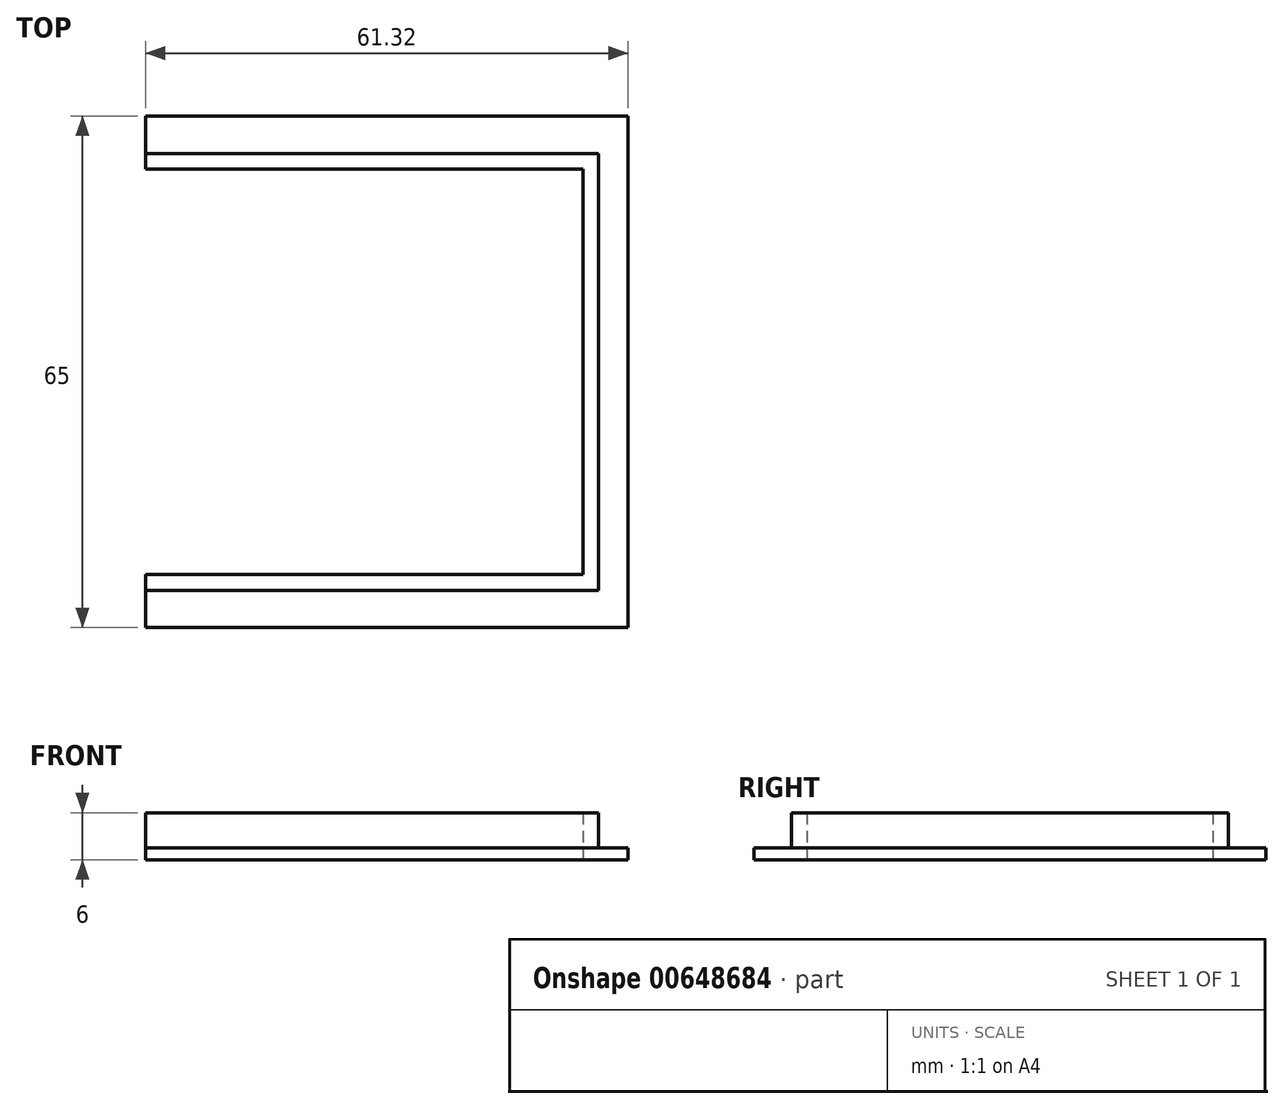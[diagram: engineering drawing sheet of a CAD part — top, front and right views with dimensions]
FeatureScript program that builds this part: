
annotation { "Feature Type Name" : "Feature", "Feature Type Description" : "" }
export const myFeature = defineFeature(function(context is Context, id is Id, definition is map)
    precondition{}
    {
        {
            var Q0;
            Q0=qCreatedBy(makeId("Top.planeOp"),FACE);
            var sketch = newSketch(context, id + "F0", { "sketchPlane" : qUnion([Q0])});
            skLineSegment(sketch, "E0.bottom", {"start": v(29.25, -25.75) * mm, "end": v(-29.25, -25.75) * mm});
            skLineSegment(sketch, "E0.top", {"start": v(29.25, 25.75) * mm, "end": v(-26.32, 25.75) * mm});
            skLineSegment(sketch, "E0.left", {"start": v(29.25, -25.75) * mm, "end": v(29.25, 25.75) * mm});
            skLineSegment(sketch, "E0.right", {"start": v(-29.25, -25.75) * mm, "end": v(-29.25, 25.75) * mm});
            skPoint(sketch, "E0.middle", {"position": v(0, 0) * mm});
            skLineSegment(sketch, "E1.bottom", {"start": v(35, -32.5) * mm, "end": v(-35, -32.5) * mm});
            skLineSegment(sketch, "E1.top", {"start": v(35, 32.5) * mm, "end": v(-26.32, 32.5) * mm});
            skLineSegment(sketch, "E1.left", {"start": v(35, -32.5) * mm, "end": v(35, 32.5) * mm});
            skLineSegment(sketch, "E1.right", {"start": v(-35, -32.5) * mm, "end": v(-35, 32.5) * mm});
            skLineSegment(sketch, "E2.0", {"start": v(-31.25, -27.75) * mm, "end": v(-31.25, 27.75) * mm});
            skLineSegment(sketch, "E2.1", {"start": v(31.25, -27.75) * mm, "end": v(-31.25, -27.75) * mm});
            skLineSegment(sketch, "E2.2", {"start": v(31.25, -27.75) * mm, "end": v(31.25, 27.75) * mm});
            skLineSegment(sketch, "E2.3", {"start": v(31.25, 27.75) * mm, "end": v(-26.32, 27.75) * mm});
            skLineSegment(sketch, "E3", {"start": v(-26.32, 32.5) * mm, "end": v(-26.32, -32.5) * mm});
            skSolve(sketch);
        }
        {
            var Q0;
            Q0=makeQuery(id+"F0.imprint","IMPRINT",FACE,{"disambiguationData":[TD([[makeQuery(id+"F0.imprint","IMPRINT",EDGE,{"derivedFrom":sQuery(id+"F0.wireOp",EDGE,"E1.bottom")}),-1.0]])]});
            var Q1;
            Q1=makeQuery(id+"F0.imprint","IMPRINT",FACE,{"disambiguationData":[TD([[makeQuery(id+"F0.imprint","IMPRINT",EDGE,{"derivedFrom":sQuery(id+"F0.wireOp",EDGE,"E0.bottom")}),1.0]])]});
            extrude(context, id + "F1", {"entities" : qUnion([Q0, Q1]), "depth" : 1.5 * mm, "offsetDistance" : 25 * mm});
        }
        {
            var Q0;
            Q0=makeQuery(id+"F0.imprint","IMPRINT",FACE,{"disambiguationData":[TD([[makeQuery(id+"F0.imprint","IMPRINT",EDGE,{"derivedFrom":sQuery(id+"F0.wireOp",EDGE,"E0.bottom")}),1.0]])]});
            extrude(context, id + "F2", {"entities" : qUnion([Q0]), "operationType" : NewBodyOperationType.ADD, "depth" : 6 * mm, "offsetDistance" : 25 * mm});
        }
    });
